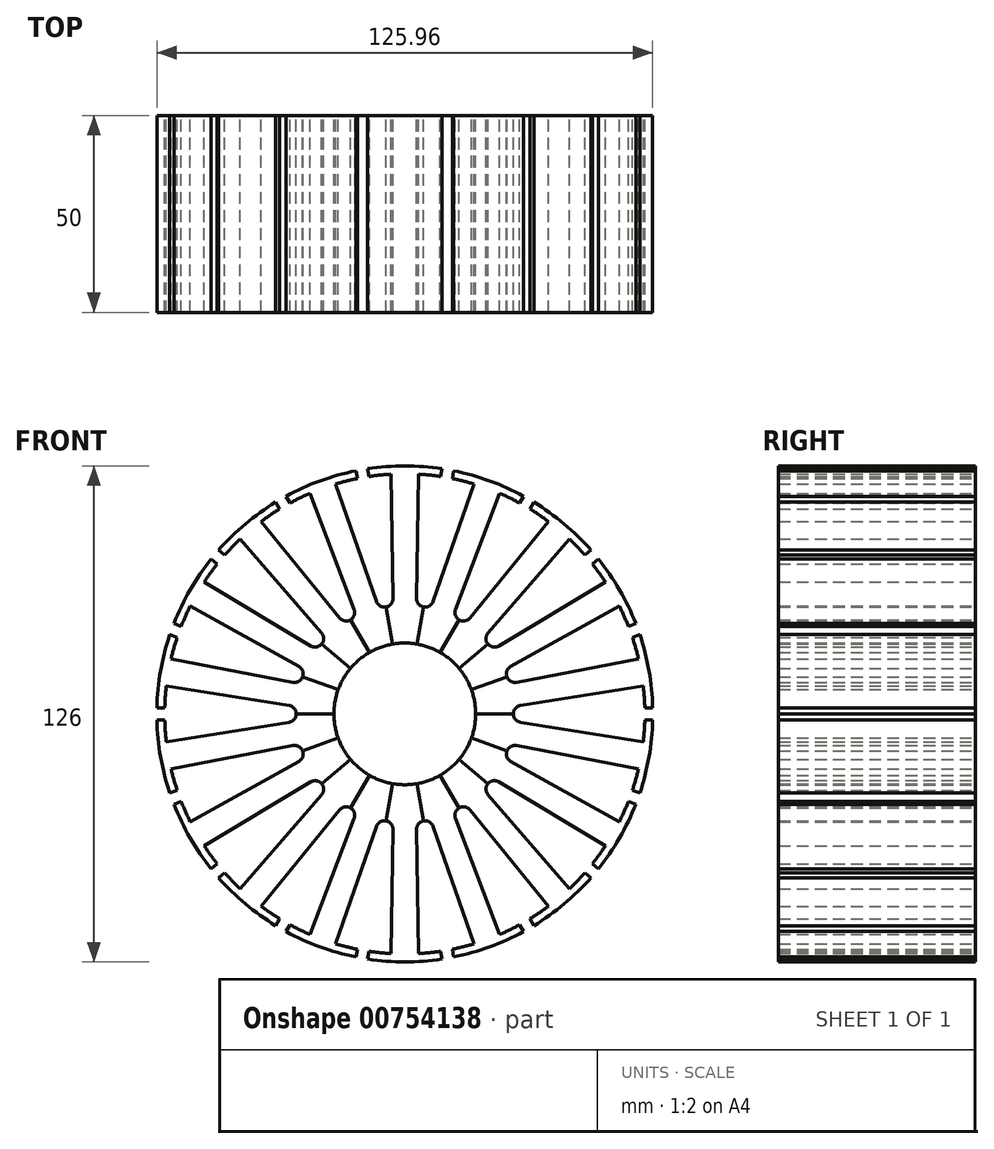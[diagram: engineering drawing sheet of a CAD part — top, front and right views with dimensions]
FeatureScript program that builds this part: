
annotation { "Feature Type Name" : "Feature", "Feature Type Description" : "" }
export const myFeature = defineFeature(function(context is Context, id is Id, definition is map)
    precondition{}
    {
        {
            var Q0;
            Q0=qCreatedBy(makeId("Front.planeOp"),FACE);
            var sketch = newSketch(context, id + "F0", { "sketchPlane" : qUnion([Q0])});
            skLineSegment(sketch, "E0", {"start": v(1.84, 29.2) * mm, "end": v(1.85, 29.2) * mm});
            skCircle(sketch, "E1", {"center": v(0, 0) * mm, "radius": 18 * mm});
            skLineSegment(sketch, "E2.MirrorCS", {"start": v(9.11, 60.32) * mm, "end": v(9.46, 62.29) * mm});
            skPoint(sketch, "E3.MirrorCS.end.orphan", {"position": v(9.11, 60.32) * mm});
            skArc(sketch, "E4", {"start": v(-9.46, 62.29) * mm, "mid": v(0, 63) * mm, "end": v(9.46, 62.29) * mm});
            skArc(sketch, "E5.trimOffspring", {"start": v(3.5, 60.9) * mm, "mid": v(6.31, 60.67) * mm, "end": v(9.11, 60.32) * mm});
            skArc(sketch, "E6.MirrorCS", {"start": v(30.2, 55.3) * mm, "mid": v(21.55, 59.2) * mm, "end": v(12.41, 61.76) * mm});
            skLineSegment(sketch, "E7.MirrorCS", {"start": v(12.07, 59.8) * mm, "end": v(12.41, 61.76) * mm});
            skArc(sketch, "E8.MirrorCS", {"start": v(18.52, 58.12) * mm, "mid": v(15.31, 59.05) * mm, "end": v(12.07, 59.8) * mm});
            skLineSegment(sketch, "E9.MirrorCS", {"start": v(29.2, 53.56) * mm, "end": v(30.2, 55.3) * mm});
            skArc(sketch, "E10.MirrorCS", {"start": v(29.2, 53.56) * mm, "mid": v(26.23, 55.07) * mm, "end": v(23.18, 56.42) * mm});
            skLineSegment(sketch, "E11.MirrorCS", {"start": v(23.19, 56.44) * mm, "end": v(11.72, 26.82) * mm});
            skArc(sketch, "E12.MirrorCS", {"start": v(17.37, 23.56) * mm, "mid": v(13.21, 22.88) * mm, "end": v(11.72, 26.82) * mm});
            skLineSegment(sketch, "E13", {"start": v(5.17, 29.3) * mm, "end": v(0, 0) * mm});
            skLineSegment(sketch, "E14.MirrorCS", {"start": v(-9.11, 60.32) * mm, "end": v(-9.46, 62.29) * mm});
            skArc(sketch, "E15.MirrorCS", {"start": v(-3.5, 60.9) * mm, "mid": v(-6.31, 60.67) * mm, "end": v(-9.11, 60.32) * mm});
            skLineSegment(sketch, "E16.MirrorCS", {"start": v(-5.17, 29.3) * mm, "end": v(0, 0) * mm});
            skLineSegment(sketch, "E17", {"start": v(0, 0) * mm, "end": v(0, 61) * mm});
            skLineSegment(sketch, "E18", {"start": v(0, 61) * mm, "end": v(0, 63) * mm});
            skPoint(sketch, "E19.trimOffspring.start.orphan", {"position": v(-3.5, 60.9) * mm});
            skLineSegment(sketch, "E20.trimOffspring", {"start": v(-2.48, 60.95) * mm, "end": v(-2.48, 60.97) * mm});
            skArc(sketch, "E21", {"start": v(3, 29.33) * mm, "mid": v(4.79, 27.16) * mm, "end": v(7.21, 28.59) * mm});
            skLineSegment(sketch, "E22", {"start": v(3.5, 60.9) * mm, "end": v(3, 29.33) * mm});
            skLineSegment(sketch, "E23.MirrorCS", {"start": v(-3.5, 60.9) * mm, "end": v(-3, 29.33) * mm});
            skLineSegment(sketch, "E24.MirrorCS", {"start": v(17.54, 58.42) * mm, "end": v(7.21, 28.59) * mm});
            skArc(sketch, "E25.MirrorCS", {"start": v(-3, 29.33) * mm, "mid": v(-4.79, 27.16) * mm, "end": v(-7.21, 28.59) * mm});
            skSolve(sketch);
        }
        {
            var Q0;
            Q0=qSketchRegion(id+"F0",true);
            extrude(context, id + "F1", {"entities" : qUnion([Q0]), "depth" : 50 * mm, "offsetDistance" : 25 * mm});
        }
        {
            var Q0;
            Q0=makeQuery(id+"F1.opExtrude","SWEPT_BODY",BODY,{"disambiguationData":[OSD([sQuery(id+"F0.wireOp",EDGE,"E1"),sQuery(id+"F0.wireOp",EDGE,"E2.MirrorCS"),sQuery(id+"F0.wireOp",EDGE,"E4"),sQuery(id+"F0.wireOp",EDGE,"E5.trimOffspring"),sQuery(id+"F0.wireOp",EDGE,"ca318c0e-4189-454f-9dea-1a5381954448"),sQuery(id+"F0.wireOp",EDGE,"c7722bac-a157-49f2-8bf4-1696ca070b5b0.MirrorCS"),sQuery(id+"F0.wireOp",EDGE,"E13"),sQuery(id+"F0.wireOp",EDGE,"c34d25b5-65db-4960-bdee-db0d58fd8b110.MirrorCS"),sQuery(id+"F0.wireOp",EDGE,"E15.MirrorCS"),sQuery(id+"F0.wireOp",EDGE,"E14.MirrorCS"),sQuery(id+"F0.wireOp",EDGE,"E16.MirrorCS"),sQuery(id+"F0.wireOp",EDGE,"311e7960-b77b-490e-97ec-5ee5712d31240.MirrorCS")])]});
            var Q1;
            Q1=makeQuery(id+"F1.opExtrude","SWEPT_FACE",FACE,{"disambiguationData":[OSD([sQuery(id+"F0.wireOp",EDGE,"E1")])]});
            circularPattern(context, id + "F2", {"entities" : qUnion([Q0]), "axis" : qUnion([Q1]), "angle" : 360 * degree, "instanceCount" : 18, "equalSpace" : true});
        }
        {
            var Q0;
            {var subQ0=sQuery(id+"F0.wireOp",EDGE,"E13");var subQ1=sQuery(id+"F0.wireOp",EDGE,"E1");var subQ2=makeQuery(id+"F0.imprint","INTERSECT",VERTEX,{"derivedFrom":[subQ1,subQ0]});Q0=makeQuery(id+"F0.imprint","IMPRINT",FACE,{"disambiguationData":[TD([[makeQuery(id+"F0.imprint","IMPRINT",EDGE,{"disambiguationData":[TD([[subQ2,1.0]])],"derivedFrom":subQ1}),1.0]])]});}
            var Q1;
            {var subQ0=sQuery(id+"F0.wireOp",EDGE,"E13");var subQ1=sQuery(id+"F0.wireOp",EDGE,"E1");var subQ2=makeQuery(id+"F0.imprint","INTERSECT",VERTEX,{"derivedFrom":[subQ1,subQ0]});Q1=makeQuery(id+"F0.imprint","IMPRINT",FACE,{"disambiguationData":[TD([[makeQuery(id+"F0.imprint","IMPRINT",EDGE,{"disambiguationData":[TD([[subQ2,-1.0]])],"derivedFrom":subQ1}),1.0]])]});}
            var Q2;
            {var subQ0=sQuery(id+"F0.wireOp",EDGE,"E16.MirrorCS");var subQ1=sQuery(id+"F0.wireOp",EDGE,"E1");var subQ2=makeQuery(id+"F0.imprint","INTERSECT",VERTEX,{"derivedFrom":[subQ1,subQ0]});Q2=makeQuery(id+"F0.imprint","IMPRINT",FACE,{"disambiguationData":[TD([[makeQuery(id+"F0.imprint","IMPRINT",EDGE,{"disambiguationData":[TD([[subQ2,1.0]])],"derivedFrom":subQ1}),1.0]])]});}
            extrude(context, id + "F3", {"entities" : qUnion([Q0, Q1, Q2]), "operationType" : NewBodyOperationType.REMOVE, "depth" : 79.3 * mm, "offsetDistance" : 25 * mm});
        }
    });
